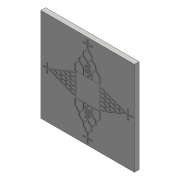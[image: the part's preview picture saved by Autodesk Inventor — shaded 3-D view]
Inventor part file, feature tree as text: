
AUTODESK INVENTOR PART (.ipt)
format: ipt  version: 2016 (Build 200138000, 138)  size: 709,120 bytes
history: native  units: mm
features: sketch x3, extrude x3, other x1
ambient origin geometry x8: Origin, YZ Plane, XZ Plane, XY Plane, X Axis, Y Axis, Z Axis, Center Point
bodies: Body1 (feature_tree)
feature tree (7):
  other  "Sólido1"
  sketch  "Boceto1"  dims[d0=5.0mm d1=0.0mm d2=0.2mm d3=0.0mm]
  extrude  "Extrusión1"  Depth=0.2mm TaperAngle=0.0deg
  extrude  "Extrusión2"  Depth=0.7mm
  extrude  "Extrusión3"  Depth=0.2mm
  sketch  "Boceto2"  dims[d4=0.7mm d5=0.7mm]
  sketch  "Boceto3"  dims[d6=0.7mm d7=0.7mm d8=0.7mm d9=0.7mm d10=0.7mm d11=0.7mm d12=0.7mm d13=0.7mm d14=0.7mm d15=0.7mm d16=0.2mm d17=0.0mm]
